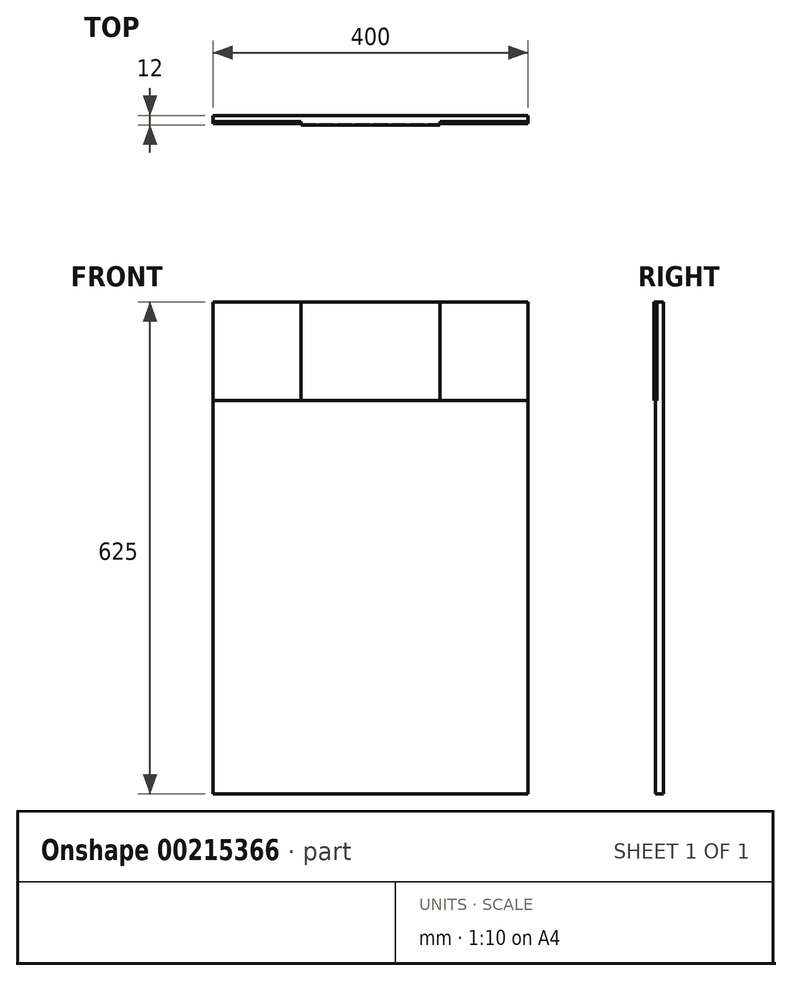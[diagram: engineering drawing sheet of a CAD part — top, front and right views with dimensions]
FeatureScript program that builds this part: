
annotation { "Feature Type Name" : "Feature", "Feature Type Description" : "" }
export const myFeature = defineFeature(function(context is Context, id is Id, definition is map)
    precondition{}
    {
        {
            var Q0;
            Q0=qCreatedBy(makeId("Front.planeOp"),FACE);
            var sketch = newSketch(context, id + "F0", { "sketchPlane" : qUnion([Q0])});
            skLineSegment(sketch, "E0.bottom", {"start": v(-200, -312.5) * mm, "end": v(200, -312.5) * mm});
            skLineSegment(sketch, "E0.top", {"start": v(-200, 312.5) * mm, "end": v(200, 312.5) * mm});
            skLineSegment(sketch, "E0.left", {"start": v(-200, -312.5) * mm, "end": v(-200, 312.5) * mm});
            skLineSegment(sketch, "E0.right", {"start": v(200, -312.5) * mm, "end": v(200, 312.5) * mm});
            skPoint(sketch, "E0.middle", {"position": v(0, 0) * mm});
            skLineSegment(sketch, "E1", {"start": v(-200, 187.5) * mm, "end": v(200, 187.5) * mm});
            skLineSegment(sketch, "E2", {"start": v(-88, 187.5) * mm, "end": v(-88, 312.5) * mm});
            skLineSegment(sketch, "E3", {"start": v(88, 187.5) * mm, "end": v(88, 312.5) * mm});
            skSolve(sketch);
        }
        {
            var Q0;
            {var subQ3=sQuery(id+"F0.wireOp",EDGE,"E2");Q0=makeQuery(id+"F0.imprint","IMPRINT",FACE,{"disambiguationData":[TD([[makeQuery(id+"F0.imprint","IMPRINT",EDGE,{"derivedFrom":subQ3}),1.0]])]});}
            var Q1;
            {var subQ3=sQuery(id+"F0.wireOp",EDGE,"E3");Q1=makeQuery(id+"F0.imprint","IMPRINT",FACE,{"disambiguationData":[TD([[makeQuery(id+"F0.imprint","IMPRINT",EDGE,{"derivedFrom":subQ3}),-1.0]])]});}
            extrude(context, id + "F1", {"entities" : qUnion([Q0, Q1]), "depth" : 8 * mm});
        }
        {
            var Q0;
            {var subQ5=sQuery(id+"F0.wireOp",EDGE,"E0.bottom");Q0=makeQuery(id+"F0.imprint","IMPRINT",FACE,{"disambiguationData":[TD([[makeQuery(id+"F0.imprint","IMPRINT",EDGE,{"derivedFrom":subQ5}),1.0]])]});}
            extrude(context, id + "F2", {"entities" : qUnion([Q0]), "operationType" : NewBodyOperationType.ADD, "depth" : 10 * mm});
        }
        {
            var Q0;
            {var subQ0=sQuery(id+"F0.wireOp",EDGE,"E2");Q0=makeQuery(id+"F0.imprint","IMPRINT",FACE,{"disambiguationData":[TD([[makeQuery(id+"F0.imprint","IMPRINT",EDGE,{"derivedFrom":subQ0}),-1.0]])]});}
            extrude(context, id + "F3", {"entities" : qUnion([Q0]), "operationType" : NewBodyOperationType.ADD, "depth" : 12 * mm});
        }
    });
